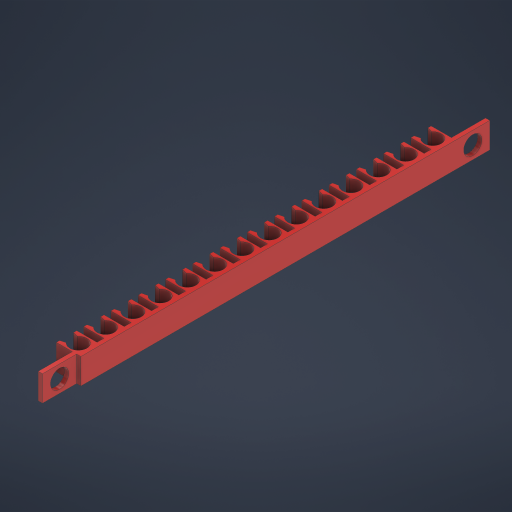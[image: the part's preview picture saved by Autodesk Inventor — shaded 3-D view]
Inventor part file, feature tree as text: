
AUTODESK INVENTOR PART (.ipt)
format: ipt  version: 2024 (Build 280153000, 153)  size: 427,008 bytes
history: native  units: in
note: dims shown in document units (in); Inventor stores cm internally (conversion verified against a paired STEP export)
features: sketch x2, extrude x1, hole x1
ambient origin geometry x8: Origin, YZ Plane, XZ Plane, XY Plane, X Axis, Y Axis, Z Axis, Center Point
bodies: Solid1 (feature_tree)
feature tree (4):
  extrude  "Extrusion1"  Depth=0.2975in
  hole  "Hole1"  [1 undecoded]
  sketch  "Sketch1"  dims[d1=0.2975in d5=0.7146in]
  sketch  "Sketch2"  dims[d6=0.7146in d7=0.125in d8=0.08in d9=0.0625in d10=0.1in d11=0.3in d12=0.05in d14=5.5118in d16=0.4in d17=0.3937in d19=1.0in d21=0.375in d22=0.0in d25=5.6in d26=2.8in d27=0.5in d28=0.0625in d29=0.0625in d30=0.375in d31=0.1875in d34=0.266in d35=0.75in d36=0.507in d37=0.25in d38=0.5635in d39=1.0in d40=0.8108in d41=0.5in d42=6.0in d43=6.5in d44=0.25in]
note: 1 required parameter value undecoded (feature->parameter linkage not recoverable at this tier; creation-order binding heuristic only, values carry confidence <= 0.55)
